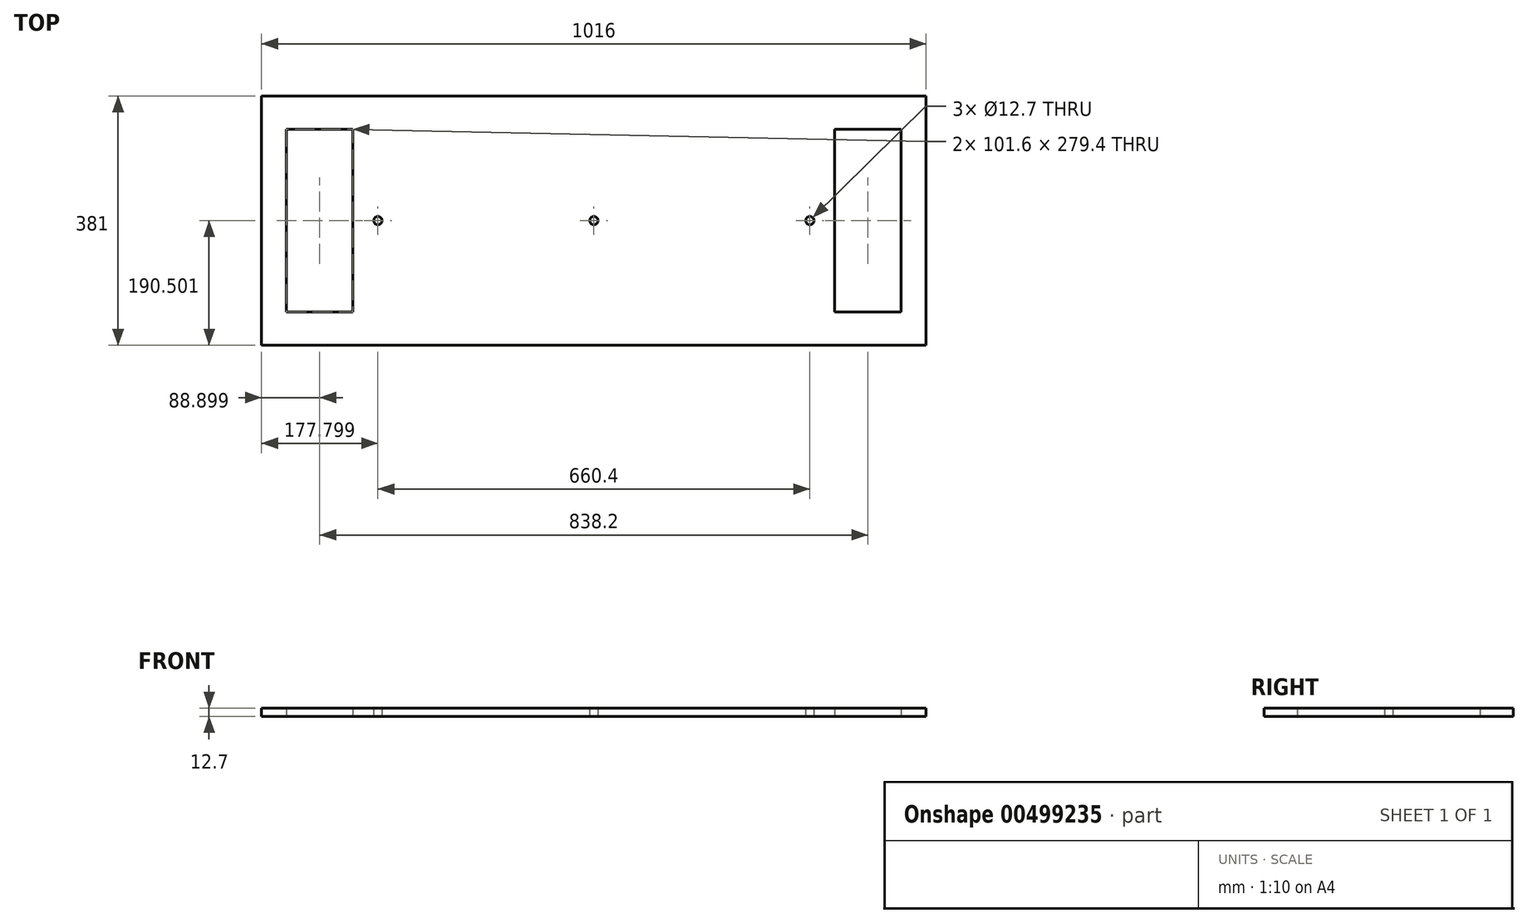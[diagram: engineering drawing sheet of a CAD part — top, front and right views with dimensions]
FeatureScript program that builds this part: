
annotation { "Feature Type Name" : "Feature", "Feature Type Description" : "" }
export const myFeature = defineFeature(function(context is Context, id is Id, definition is map)
    precondition{}
    {
        {
            var Q0;
            Q0=qCreatedBy(makeId("Top.planeOp"),FACE);
            var sketch = newSketch(context, id + "F0", { "sketchPlane" : qUnion([Q0])});
            skLineSegment(sketch, "E0.bottom", {"start": v(-383.02, 174.33) * mm, "end": v(632.98, 174.33) * mm});
            skLineSegment(sketch, "E0.top", {"start": v(-383.02, -206.67) * mm, "end": v(632.98, -206.67) * mm});
            skLineSegment(sketch, "E0.left", {"start": v(-383.02, 174.33) * mm, "end": v(-383.02, -206.67) * mm});
            skLineSegment(sketch, "E0.right", {"start": v(632.98, 174.33) * mm, "end": v(632.98, -206.67) * mm});
            skLineSegment(sketch, "E1", {"start": v(-344.92, -16.17) * mm, "end": v(-344.92, 123.53) * mm});
            skLineSegment(sketch, "E2", {"start": v(-344.92, 123.53) * mm, "end": v(-243.32, 123.53) * mm});
            skLineSegment(sketch, "E3", {"start": v(-243.32, 123.53) * mm, "end": v(-243.32, -155.87) * mm});
            skLineSegment(sketch, "E4", {"start": v(-243.32, -155.87) * mm, "end": v(-344.92, -155.87) * mm});
            skLineSegment(sketch, "E5", {"start": v(-344.92, -155.87) * mm, "end": v(-344.92, -16.17) * mm});
            skLineSegment(sketch, "E6", {"start": v(124.98, -206.67) * mm, "end": v(124.98, 174.33) * mm, "construction": true});
            skLineSegment(sketch, "E7.MirrorCS", {"start": v(493.28, 123.53) * mm, "end": v(493.28, -155.87) * mm});
            skLineSegment(sketch, "E8.MirrorCS", {"start": v(493.28, -155.87) * mm, "end": v(594.88, -155.87) * mm});
            skLineSegment(sketch, "E9.MirrorCS", {"start": v(594.88, -155.87) * mm, "end": v(594.88, -16.17) * mm});
            skLineSegment(sketch, "E10.MirrorCS", {"start": v(594.88, -16.17) * mm, "end": v(594.88, 123.53) * mm});
            skLineSegment(sketch, "E11.MirrorCS", {"start": v(594.88, 123.53) * mm, "end": v(493.28, 123.53) * mm});
            skLineSegment(sketch, "E12", {"start": v(-243.32, -16.17) * mm, "end": v(-205.22, -16.17) * mm, "construction": true});
            skCircle(sketch, "E13", {"center": v(-205.22, -16.17) * mm, "radius": 6.35 * mm});
            skCircle(sketch, "E14.MirrorC", {"center": v(455.18, -16.17) * mm, "radius": 6.35 * mm});
            skCircle(sketch, "E15", {"center": v(124.98, -16.17) * mm, "radius": 6.35 * mm});
            skSolve(sketch);
        }
        {
            var Q0;
            Q0 = qSketchRegion(id + "F0", true);
            extrude(context, id + "F1", {"entities" : qUnion([Q0]), "depth" : 12.7 * mm, "offsetDistance" : 25.4 * mm});
        }
    });
